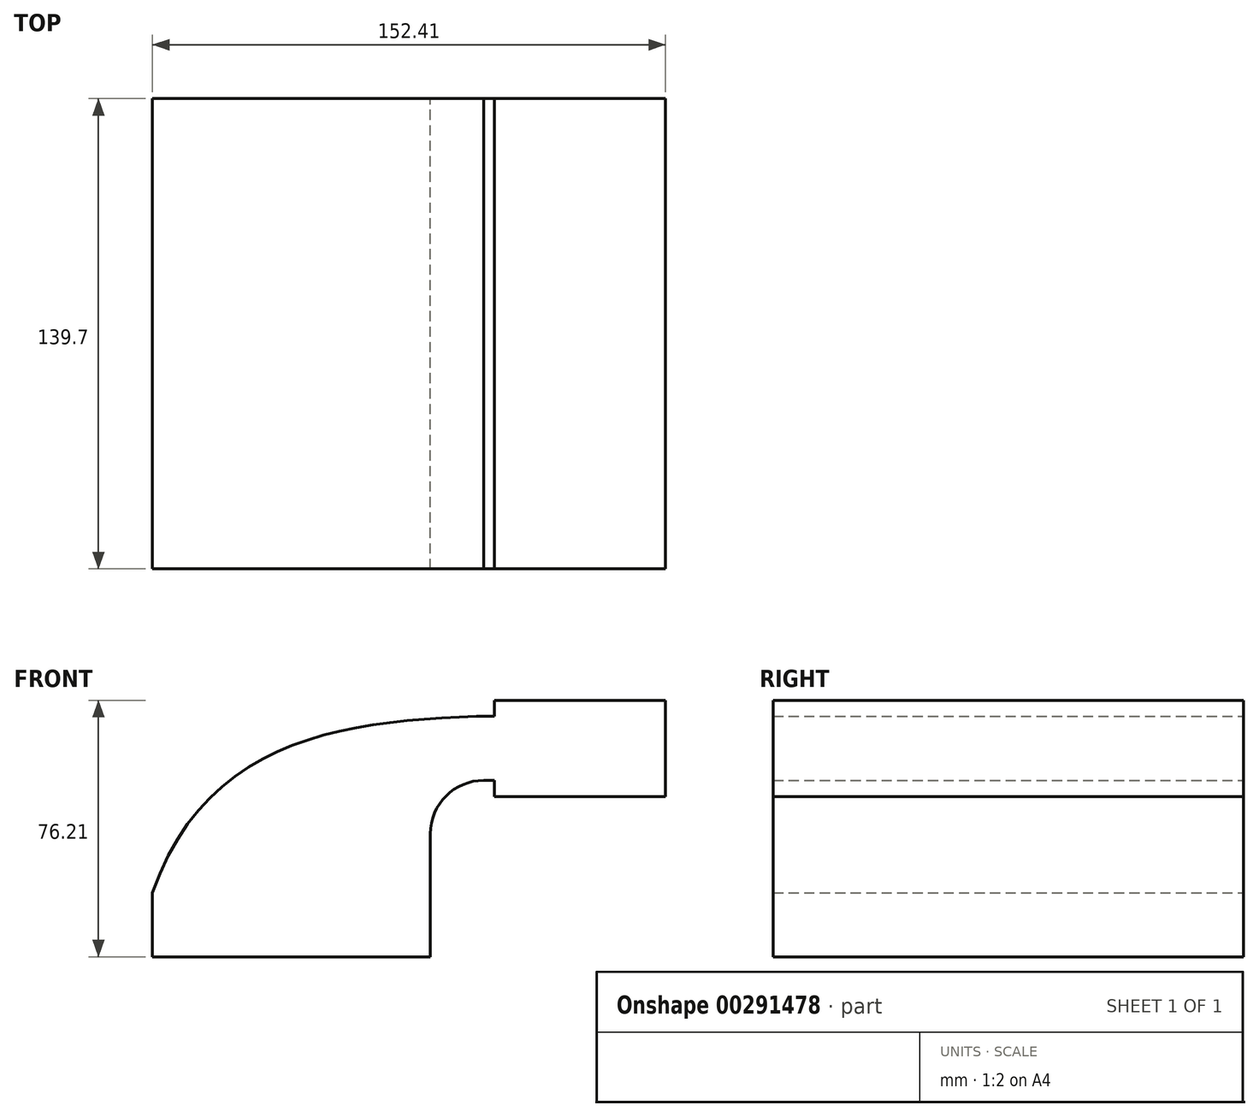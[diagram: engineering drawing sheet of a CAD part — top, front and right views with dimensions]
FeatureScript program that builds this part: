
annotation { "Feature Type Name" : "Feature", "Feature Type Description" : "" }
export const myFeature = defineFeature(function(context is Context, id is Id, definition is map)
    precondition{}
    {
        {
            var Q0;
            Q0=qCreatedBy(makeId("Front.planeOp"),FACE);
            var sketch = newSketch(context, id + "F0", { "sketchPlane" : qUnion([Q0])});
            skLineSegment(sketch, "E0.bottom", {"start": v(41.27, 9.53) * mm, "end": v(-41.28, 9.53) * mm});
            skLineSegment(sketch, "E0.top", {"start": v(41.28, -9.52) * mm, "end": v(-41.27, -9.52) * mm});
            skLineSegment(sketch, "E0.left", {"start": v(41.27, 9.53) * mm, "end": v(41.28, -9.52) * mm});
            skLineSegment(sketch, "E0.right", {"start": v(-41.28, 9.53) * mm, "end": v(-41.27, -9.52) * mm});
            skPoint(sketch, "E0.middle", {"position": v(0, 0) * mm});
            skLineSegment(sketch, "E1.bottom", {"start": v(60.32, 66.68) * mm, "end": v(111.12, 66.68) * mm});
            skLineSegment(sketch, "E1.top", {"start": v(60.32, 38.1) * mm, "end": v(111.12, 38.1) * mm});
            skLineSegment(sketch, "E1.left", {"start": v(60.32, 66.68) * mm, "end": v(60.32, 38.1) * mm});
            skLineSegment(sketch, "E1.right", {"start": v(111.12, 66.68) * mm, "end": v(111.12, 38.1) * mm});
            skPoint(sketch, "E1.middle", {"position": v(85.72, 52.39) * mm});
            skLineSegment(sketch, "E2", {"start": v(41.27, 9.53) * mm, "end": v(41.27, 27) * mm});
            skArc(sketch, "E3", {"start": v(41.27, 27) * mm, "mid": v(45.92, 38.23) * mm, "end": v(57.15, 42.88) * mm});
            skLineSegment(sketch, "E4", {"start": v(57.15, 42.88) * mm, "end": v(85.72, 42.88) * mm});
            skPoint(sketch, "E4.endSnap0", {"position": v(85.72, 38.1) * mm});
            skLineSegment(sketch, "E5.0", {"start": v(57.15, 61.93) * mm, "end": v(85.72, 61.93) * mm});
            skArc(sketch, "E5.1", {"start": v(22.22, 27) * mm, "mid": v(32.45, 51.7) * mm, "end": v(57.15, 61.93) * mm});
            skLineSegment(sketch, "E5.2", {"start": v(22.22, 9.53) * mm, "end": v(22.22, 27) * mm});
            skLineSegment(sketch, "E6", {"start": v(85.72, 38.1) * mm, "end": v(85.72, 66.68) * mm});
            skFitSpline(sketch, "E7", {"points": [v(-41.28, 9.52) * mm, v(57.15, 61.93) * mm], "startDerivative": vector(48.64, 139.3) * mm, "endDerivative": vector(121.06, 3.52) * mm});
            skSolve(sketch);
        }
        {
            var Q0;
            {var subQ0=sQuery(id+"F0.wireOp",EDGE,"E1.left");var subQ1=sQuery(id+"F0.wireOp",EDGE,"E1.bottom");var subQ2=makeQuery(id+"F0.imprint","INTERSECT",VERTEX,{"derivedFrom":[subQ1,subQ0]});Q0=makeQuery(id+"F0.imprint","IMPRINT",FACE,{"disambiguationData":[TD([[makeQuery(id+"F0.imprint","IMPRINT",EDGE,{"disambiguationData":[TD([[subQ2,-1.0]])],"derivedFrom":subQ1}),-1.0]])]});}
            var Q1;
            {var subQ0=sQuery(id+"F0.wireOp",EDGE,"E1.left");var subQ1=sQuery(id+"F0.wireOp",EDGE,"E1.top");var subQ2=makeQuery(id+"F0.imprint","INTERSECT",VERTEX,{"derivedFrom":[subQ1,subQ0]});Q1=makeQuery(id+"F0.imprint","IMPRINT",FACE,{"disambiguationData":[TD([[makeQuery(id+"F0.imprint","IMPRINT",EDGE,{"disambiguationData":[TD([[subQ2,-1.0]])],"derivedFrom":subQ1}),1.0]])]});}
            var Q2;
            {var subQ1=sQuery(id+"F0.wireOp",EDGE,"E2");Q2=makeQuery(id+"F0.imprint","IMPRINT",FACE,{"disambiguationData":[TD([[makeQuery(id+"F0.imprint","IMPRINT",EDGE,{"derivedFrom":subQ1}),1.0]])]});}
            var Q3;
            {var subQ0=sQuery(id+"F0.wireOp",EDGE,"E5.0");var subQ1=sQuery(id+"F0.wireOp",EDGE,"E1.left");var subQ2=makeQuery(id+"F0.imprint","INTERSECT",VERTEX,{"derivedFrom":[subQ1,subQ0]});Q3=makeQuery(id+"F0.imprint","IMPRINT",FACE,{"disambiguationData":[TD([[makeQuery(id+"F0.imprint","IMPRINT",EDGE,{"disambiguationData":[TD([[subQ2,-1.0]])],"derivedFrom":subQ1}),1.0]])]});}
            var Q4;
            {var subQ4=sQuery(id+"F0.wireOp",EDGE,"E1.right");Q4=makeQuery(id+"F0.imprint","IMPRINT",FACE,{"disambiguationData":[TD([[makeQuery(id+"F0.imprint","IMPRINT",EDGE,{"derivedFrom":subQ4}),-1.0]])]});}
            var Q5;
            {var subQ0=sQuery(id+"F0.wireOp",EDGE,"E5.0");var subQ1=sQuery(id+"F0.wireOp",EDGE,"E1.left");var subQ2=makeQuery(id+"F0.imprint","INTERSECT",VERTEX,{"derivedFrom":[subQ1,subQ0]});Q5=makeQuery(id+"F0.imprint","IMPRINT",FACE,{"disambiguationData":[TD([[makeQuery(id+"F0.imprint","IMPRINT",EDGE,{"disambiguationData":[TD([[subQ2,-1.0]])],"derivedFrom":subQ1}),1.0]])]});}
            var Q6;
            {var subQ0=sQuery(id+"F0.wireOp",EDGE,"E1.left");var subQ1=sQuery(id+"F0.wireOp",EDGE,"E1.top");var subQ2=makeQuery(id+"F0.imprint","INTERSECT",VERTEX,{"derivedFrom":[subQ1,subQ0]});Q6=makeQuery(id+"F0.imprint","IMPRINT",FACE,{"disambiguationData":[TD([[makeQuery(id+"F0.imprint","IMPRINT",EDGE,{"disambiguationData":[TD([[subQ2,-1.0]])],"derivedFrom":subQ1}),1.0]])]});}
            var Q7;
            {var subQ1=sQuery(id+"F0.wireOp",EDGE,"E2");Q7=makeQuery(id+"F0.imprint","IMPRINT",FACE,{"disambiguationData":[TD([[makeQuery(id+"F0.imprint","IMPRINT",EDGE,{"derivedFrom":subQ1}),1.0]])]});}
            var Q8;
            {var subQ0=sQuery(id+"F0.wireOp",EDGE,"E7");var subQ1=sQuery(id+"F0.wireOp",EDGE,"E5.1");var subQ3=makeQuery(id+"F0.imprint","INTERSECT",VERTEX,{"derivedFrom":[subQ1,subQ0]});Q8=makeQuery(id+"F0.imprint","IMPRINT",FACE,{"disambiguationData":[TD([[makeQuery(id+"F0.imprint","IMPRINT",EDGE,{"disambiguationData":[TD([[subQ3,-1.0]])],"derivedFrom":subQ1}),-1.0]])]});}
            var Q9;
            {var subQ4=sQuery(id+"F0.wireOp",EDGE,"E1.right");Q9=makeQuery(id+"F0.imprint","IMPRINT",FACE,{"disambiguationData":[TD([[makeQuery(id+"F0.imprint","IMPRINT",EDGE,{"derivedFrom":subQ4}),-1.0]])]});}
            var Q10;
            Q10=makeQuery(id+"F0.imprint","IMPRINT",FACE,{"disambiguationData":[TD([[makeQuery(id+"F0.imprint","IMPRINT",EDGE,{"derivedFrom":sQuery(id+"F0.wireOp",EDGE,"E0.top")}),-1.0]])]});
            var Q11;
            {var subQ0=sQuery(id+"F0.wireOp",EDGE,"E1.left");var subQ1=sQuery(id+"F0.wireOp",EDGE,"E1.bottom");var subQ2=makeQuery(id+"F0.imprint","INTERSECT",VERTEX,{"derivedFrom":[subQ1,subQ0]});Q11=makeQuery(id+"F0.imprint","IMPRINT",FACE,{"disambiguationData":[TD([[makeQuery(id+"F0.imprint","IMPRINT",EDGE,{"disambiguationData":[TD([[subQ2,-1.0]])],"derivedFrom":subQ1}),-1.0]])]});}
            extrude(context, id + "F1", {"entities" : qUnion([Q0, Q1, Q2, Q3, Q4, Q5, Q6, Q7, Q8, Q9, Q10, Q11]), "endBound" : BoundingType.SYMMETRIC, "depth" : 50.8 * mm});
        }
        {
            var Q0;
            Q0=makeQuery(id+"F1.opExtrude","CAP_FACE",FACE,{"disambiguationData":[OSD([sQuery(id+"F0.wireOp",EDGE,"E0.bottom"),sQuery(id+"F0.wireOp",EDGE,"E0.top"),sQuery(id+"F0.wireOp",EDGE,"E0.left"),sQuery(id+"F0.wireOp",EDGE,"E0.right"),sQuery(id+"F0.wireOp",EDGE,"E1.bottom"),sQuery(id+"F0.wireOp",EDGE,"E1.top"),sQuery(id+"F0.wireOp",EDGE,"E1.left"),sQuery(id+"F0.wireOp",EDGE,"E1.right"),sQuery(id+"F0.wireOp",EDGE,"E2"),sQuery(id+"F0.wireOp",EDGE,"E3"),sQuery(id+"F0.wireOp",EDGE,"E4"),sQuery(id+"F0.wireOp",EDGE,"E5.0"),sQuery(id+"F0.wireOp",EDGE,"E5.1"),sQuery(id+"F0.wireOp",EDGE,"E5.2")])],"isStart":false});
            extrude(context, id + "F2", {"entities" : qUnion([Q0]), "operationType" : NewBodyOperationType.ADD, "endBound" : BoundingType.SYMMETRIC, "depth" : 127 * mm});
        }
        {
            var Q0;
            Q0=makeQuery(id+"F2.opExtrude","CAP_FACE",FACE,{"disambiguationData":[OSD([sQuery(id+"F0.wireOp",EDGE,"E0.bottom"),sQuery(id+"F0.wireOp",EDGE,"E0.top"),sQuery(id+"F0.wireOp",EDGE,"E0.left"),sQuery(id+"F0.wireOp",EDGE,"E0.right"),sQuery(id+"F0.wireOp",EDGE,"E1.bottom"),sQuery(id+"F0.wireOp",EDGE,"E1.top"),sQuery(id+"F0.wireOp",EDGE,"E1.left"),sQuery(id+"F0.wireOp",EDGE,"E1.right"),sQuery(id+"F0.wireOp",EDGE,"E2"),sQuery(id+"F0.wireOp",EDGE,"E3"),sQuery(id+"F0.wireOp",EDGE,"E4"),sQuery(id+"F0.wireOp",EDGE,"E5.0"),sQuery(id+"F0.wireOp",EDGE,"E5.1"),sQuery(id+"F0.wireOp",EDGE,"E5.2")])],"isStart":false});
            extrude(context, id + "F3", {"entities" : qUnion([Q0]), "operationType" : NewBodyOperationType.ADD, "endBound" : BoundingType.SYMMETRIC, "depth" : 25.4 * mm});
        }
    });
